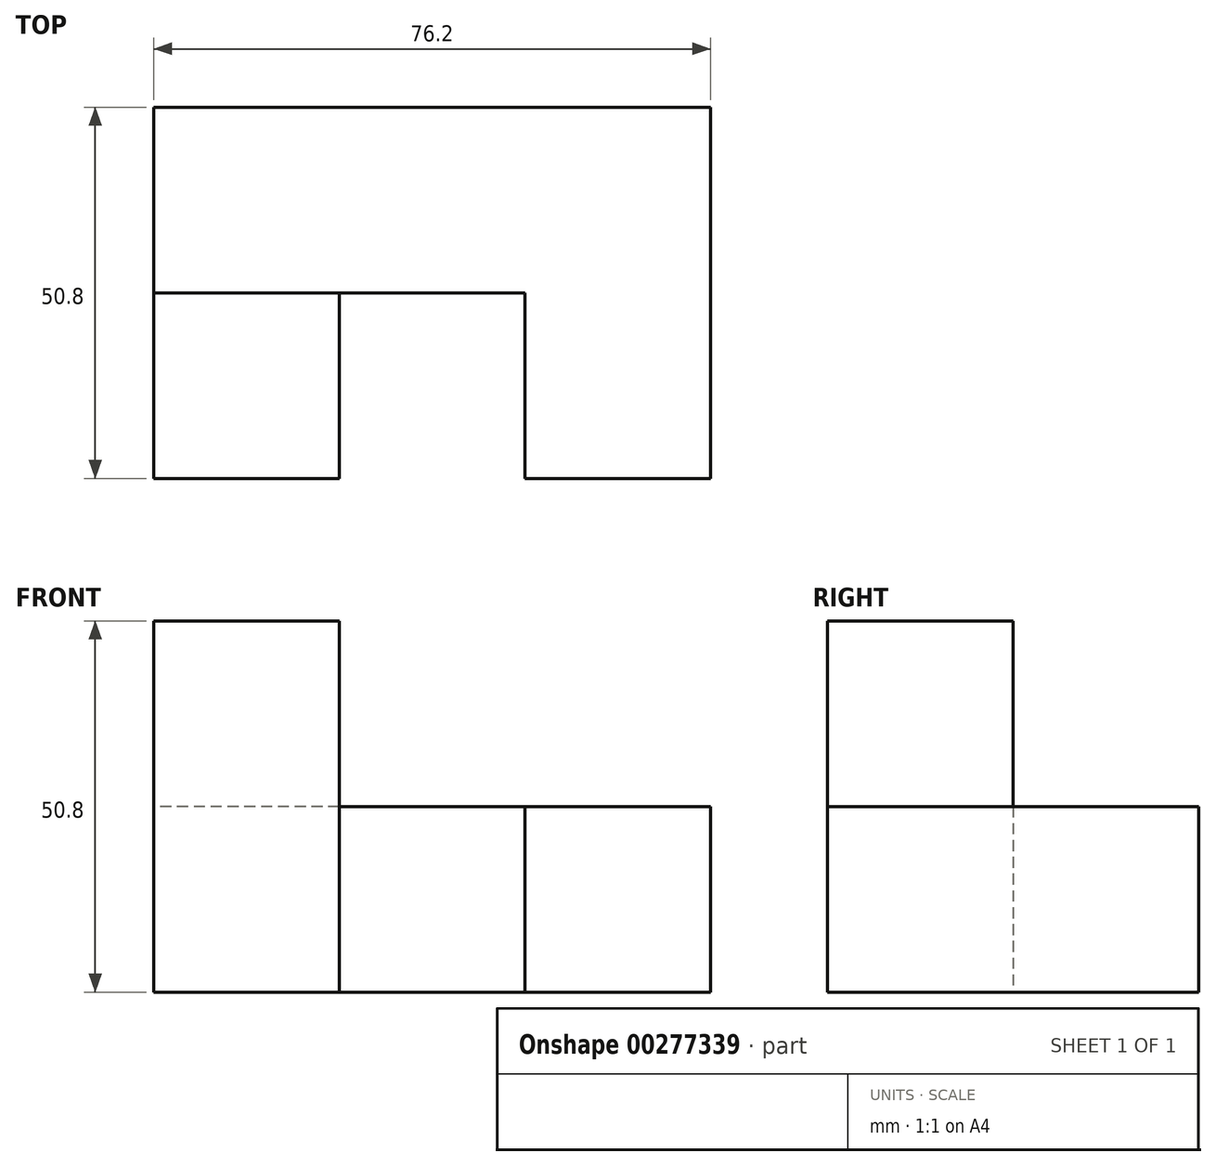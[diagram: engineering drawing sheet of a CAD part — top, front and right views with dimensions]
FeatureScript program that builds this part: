
annotation { "Feature Type Name" : "Feature", "Feature Type Description" : "" }
export const myFeature = defineFeature(function(context is Context, id is Id, definition is map)
    precondition{}
    {
        {
            var Q0;
            Q0=qCreatedBy(makeId("Front.planeOp"),FACE);
            var sketch = newSketch(context, id + "F0", { "sketchPlane" : qUnion([Q0])});
            skLineSegment(sketch, "E0", {"start": v(-39.31, -20.07) * mm, "end": v(-13.91, -20.07) * mm});
            skLineSegment(sketch, "E1", {"start": v(-13.91, -20.07) * mm, "end": v(11.49, -20.07) * mm});
            skLineSegment(sketch, "E2", {"start": v(11.49, -20.07) * mm, "end": v(36.89, -20.07) * mm});
            skLineSegment(sketch, "E3", {"start": v(36.89, -20.07) * mm, "end": v(36.89, 5.33) * mm});
            skLineSegment(sketch, "E4", {"start": v(36.89, 5.33) * mm, "end": v(11.49, 5.33) * mm});
            skLineSegment(sketch, "E5", {"start": v(11.49, 5.33) * mm, "end": v(-13.91, 5.33) * mm});
            skLineSegment(sketch, "E6", {"start": v(-13.91, 5.33) * mm, "end": v(-39.31, 5.33) * mm});
            skLineSegment(sketch, "E7", {"start": v(-39.31, 5.33) * mm, "end": v(-39.31, -20.07) * mm});
            skLineSegment(sketch, "E8", {"start": v(-13.91, 5.33) * mm, "end": v(-13.91, -20.07) * mm});
            skLineSegment(sketch, "E9", {"start": v(11.49, 5.33) * mm, "end": v(11.49, -20.07) * mm});
            skSolve(sketch);
        }
        {
            var Q0;
            Q0=makeQuery(id+"F0.imprint","IMPRINT",FACE,{"disambiguationData":[TD([[makeQuery(id+"F0.imprint","IMPRINT",EDGE,{"derivedFrom":sQuery(id+"F0.wireOp",EDGE,"E1")}),1.0]])]});
            extrude(context, id + "F1", {"entities" : qUnion([Q0]), "depth" : 25.4 * mm});
        }
        {
            var Q0;
            Q0=makeQuery(id+"F0.imprint","IMPRINT",FACE,{"disambiguationData":[TD([[makeQuery(id+"F0.imprint","IMPRINT",EDGE,{"derivedFrom":sQuery(id+"F0.wireOp",EDGE,"E0")}),1.0]])]});
            var Q1;
            Q1=makeQuery(id+"F0.imprint","IMPRINT",FACE,{"disambiguationData":[TD([[makeQuery(id+"F0.imprint","IMPRINT",EDGE,{"derivedFrom":sQuery(id+"F0.wireOp",EDGE,"E2")}),1.0]])]});
            extrude(context, id + "F2", {"entities" : qUnion([Q0, Q1]), "operationType" : NewBodyOperationType.ADD, "depth" : 50.8 * mm});
        }
        {
            var Q0;
            Q0=makeQuery(id+"F2.boolean.opBoolean","MERGE",FACE,{"derivedFrom":[makeQuery(id+"F1.opExtrude","SWEPT_FACE",FACE,{"disambiguationData":[OSD([sQuery(id+"F0.wireOp",EDGE,"E5")])]}),makeQuery(id+"F2.opExtrude","SWEPT_FACE",FACE,{"disambiguationData":[OSD([sQuery(id+"F0.wireOp",EDGE,"E4")])]}),makeQuery(id+"F2.opExtrude","SWEPT_FACE",FACE,{"disambiguationData":[OSD([sQuery(id+"F0.wireOp",EDGE,"E6")])]})]});
            var sketch = newSketch(context, id + "F3", { "sketchPlane" : qUnion([Q0])});
            skLineSegment(sketch, "E10.bottom", {"start": v(-13.91, -50.8) * mm, "end": v(-39.31, -50.8) * mm});
            skLineSegment(sketch, "E10.top", {"start": v(-13.91, -25.4) * mm, "end": v(-39.31, -25.4) * mm});
            skLineSegment(sketch, "E10.left", {"start": v(-13.91, -50.8) * mm, "end": v(-13.91, -25.4) * mm});
            skLineSegment(sketch, "E10.right", {"start": v(-39.31, -50.8) * mm, "end": v(-39.31, -25.4) * mm});
            skSolve(sketch);
        }
        {
            var Q0;
            Q0 = qSketchRegion(id + "F3", true);
            extrude(context, id + "F4", {"entities" : qUnion([Q0]), "operationType" : NewBodyOperationType.ADD, "depth" : 25.4 * mm});
        }
    });
